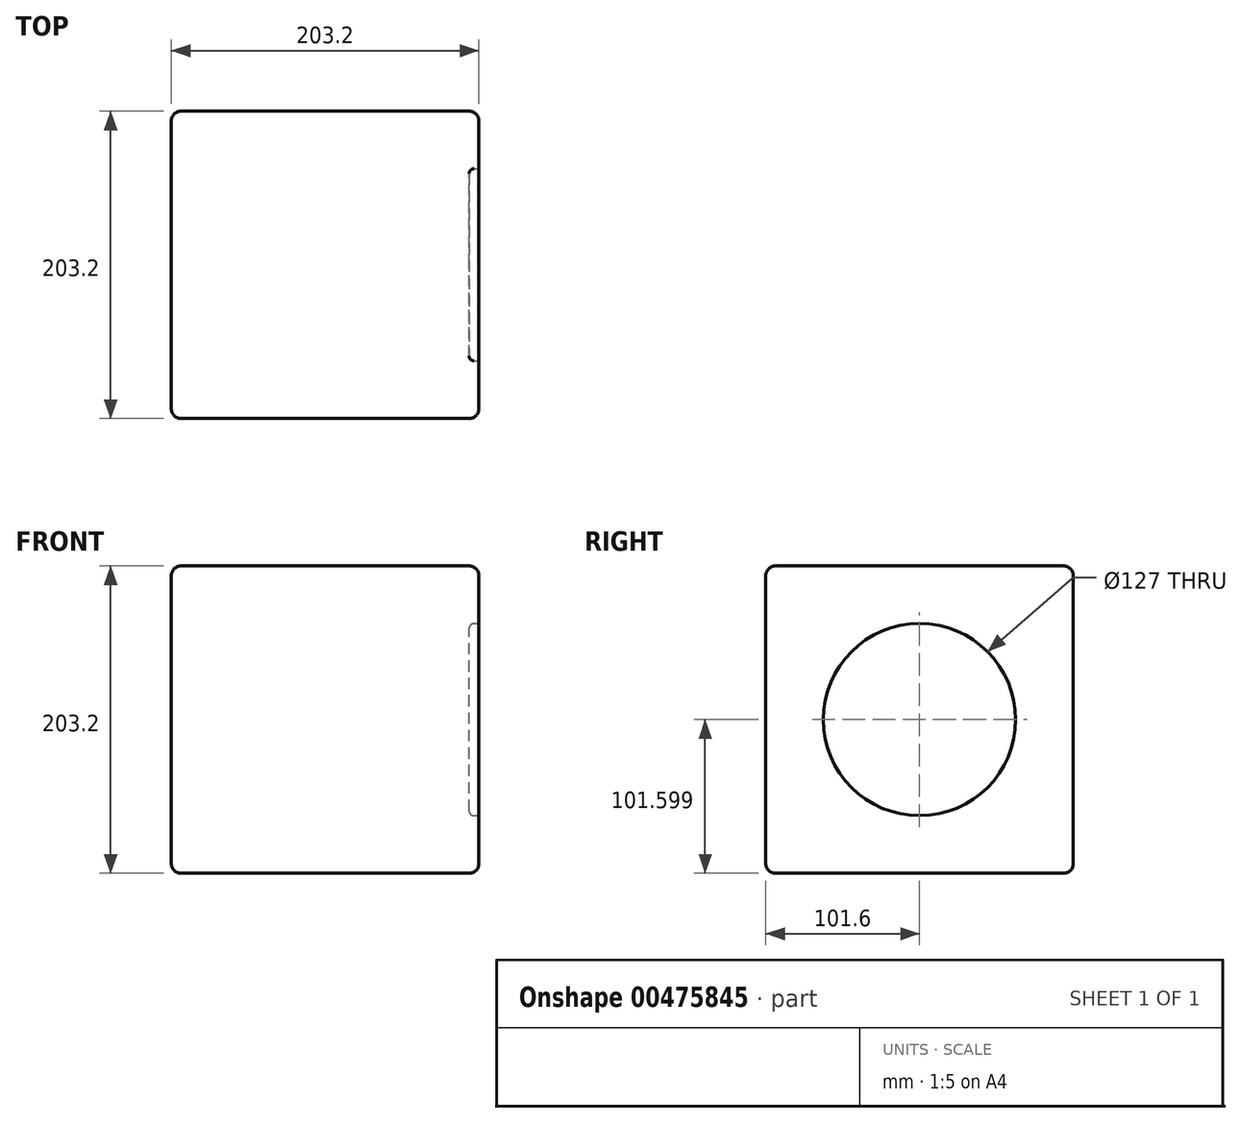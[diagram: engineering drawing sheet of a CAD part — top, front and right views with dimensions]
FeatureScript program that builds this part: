
annotation { "Feature Type Name" : "Feature", "Feature Type Description" : "" }
export const myFeature = defineFeature(function(context is Context, id is Id, definition is map)
    precondition{}
    {
        {
            var Q0;
            Q0=qCreatedBy(makeId("Front.planeOp"),FACE);
            var sketch = newSketch(context, id + "F0", { "sketchPlane" : qUnion([Q0])});
            skLineSegment(sketch, "E0.bottom", {"start": v(-159.8, -111.74) * mm, "end": v(43.4, -111.74) * mm});
            skLineSegment(sketch, "E0.top", {"start": v(-159.8, 91.46) * mm, "end": v(43.4, 91.46) * mm});
            skLineSegment(sketch, "E0.left", {"start": v(-159.8, -111.74) * mm, "end": v(-159.8, 91.46) * mm});
            skLineSegment(sketch, "E0.right", {"start": v(43.4, -111.74) * mm, "end": v(43.4, 91.46) * mm});
            skSolve(sketch);
        }
        {
            var Q0;
            Q0=makeQuery(id+"F0.imprint","IMPRINT",FACE,{"disambiguationData":[TD([[makeQuery(id+"F0.imprint","IMPRINT",EDGE,{"derivedFrom":sQuery(id+"F0.wireOp",EDGE,"E0.bottom")}),1.0]])]});
            extrude(context, id + "F1", {"entities" : qUnion([Q0]), "depth" : 203.2 * mm});
        }
        {
            var Q0;
            Q0=makeQuery(id+"F1.opExtrude","SWEPT_FACE",FACE,{"disambiguationData":[OSD([sQuery(id+"F0.wireOp",EDGE,"E0.left")])]});
            var Q1;
            Q1=makeQuery(id+"F1.opExtrude","CAP_FACE",FACE,{"disambiguationData":[OSD([sQuery(id+"F0.wireOp",EDGE,"E0.bottom"),sQuery(id+"F0.wireOp",EDGE,"E0.top"),sQuery(id+"F0.wireOp",EDGE,"E0.left"),sQuery(id+"F0.wireOp",EDGE,"E0.right")])],"isStart":true});
            var Q2;
            Q2=makeQuery(id+"F1.opExtrude","SWEPT_FACE",FACE,{"disambiguationData":[OSD([sQuery(id+"F0.wireOp",EDGE,"E0.top")])]});
            var Q3;
            Q3=makeQuery(id+"F1.opExtrude","SWEPT_FACE",FACE,{"disambiguationData":[OSD([sQuery(id+"F0.wireOp",EDGE,"E0.right")])]});
            var Q4;
            Q4=makeQuery(id+"F1.opExtrude","CAP_FACE",FACE,{"disambiguationData":[OSD([sQuery(id+"F0.wireOp",EDGE,"E0.bottom"),sQuery(id+"F0.wireOp",EDGE,"E0.top"),sQuery(id+"F0.wireOp",EDGE,"E0.left"),sQuery(id+"F0.wireOp",EDGE,"E0.right")])],"isStart":false});
            var Q5;
            Q5=makeQuery(id+"F1.opExtrude","SWEPT_FACE",FACE,{"disambiguationData":[OSD([sQuery(id+"F0.wireOp",EDGE,"E0.bottom")])]});
            fillet(context, id + "F2", {"entities" : qUnion([Q0, Q1, Q2, Q3, Q4, Q5]), "radius" : 6.35 * mm, "tangentPropagation" : true, "allowEdgeOverflow" : false});
        }
        {
            var Q0;
            Q0=makeQuery(id+"F1.opExtrude","SWEPT_FACE",FACE,{"disambiguationData":[OSD([sQuery(id+"F0.wireOp",EDGE,"E0.right")])]});
            var sketch = newSketch(context, id + "F3", { "sketchPlane" : qUnion([Q0])});
            skLineSegment(sketch, "E1", {"start": v(-6.35, 85.1) * mm, "end": v(-196.85, -105.4) * mm, "construction": true});
            skLineSegment(sketch, "E2", {"start": v(-6.35, -105.4) * mm, "end": v(-196.85, 85.1) * mm, "construction": true});
            skLineSegment(sketch, "E3", {"start": v(-196.85, 85.1) * mm, "end": v(-101.6, -10.14) * mm, "construction": true});
            skCircle(sketch, "E4", {"center": v(-101.6, -10.14) * mm, "radius": 63.5 * mm});
            skSolve(sketch);
        }
        {
            var Q0;
            Q0=makeQuery(id+"F3.imprint","IMPRINT",FACE,{"disambiguationData":[TD([[makeQuery(id+"F3.imprint","IMPRINT",EDGE,{"derivedFrom":sQuery(id+"F3.wireOp",EDGE,"E4")}),1.0]])]});
            extrude(context, id + "F4", {"entities" : qUnion([Q0]), "operationType" : NewBodyOperationType.REMOVE, "oppositeDirection" : true, "depth" : 6.35 * mm});
        }
        {
            var Q0;
            Q0=makeQuery(id+"F4.boolean.opBoolean","COPY",EDGE,{"derivedFrom":makeQuery(id+"F4.opExtrude","CAP_EDGE",EDGE,{"disambiguationData":[OSD([sQuery(id+"F3.wireOp",EDGE,"E4")])],"isStart":true})});
            var Q1;
            Q1=makeQuery(id+"F4.boolean.opBoolean","COPY",EDGE,{"derivedFrom":makeQuery(id+"F4.opExtrude","CAP_EDGE",EDGE,{"disambiguationData":[OSD([sQuery(id+"F3.wireOp",EDGE,"E4")])],"isStart":false})});
            fillet(context, id + "F5", {"entities" : qUnion([Q0, Q1]), "radius" : 3.17 * mm, "tangentPropagation" : true, "allowEdgeOverflow" : false});
        }
    });
